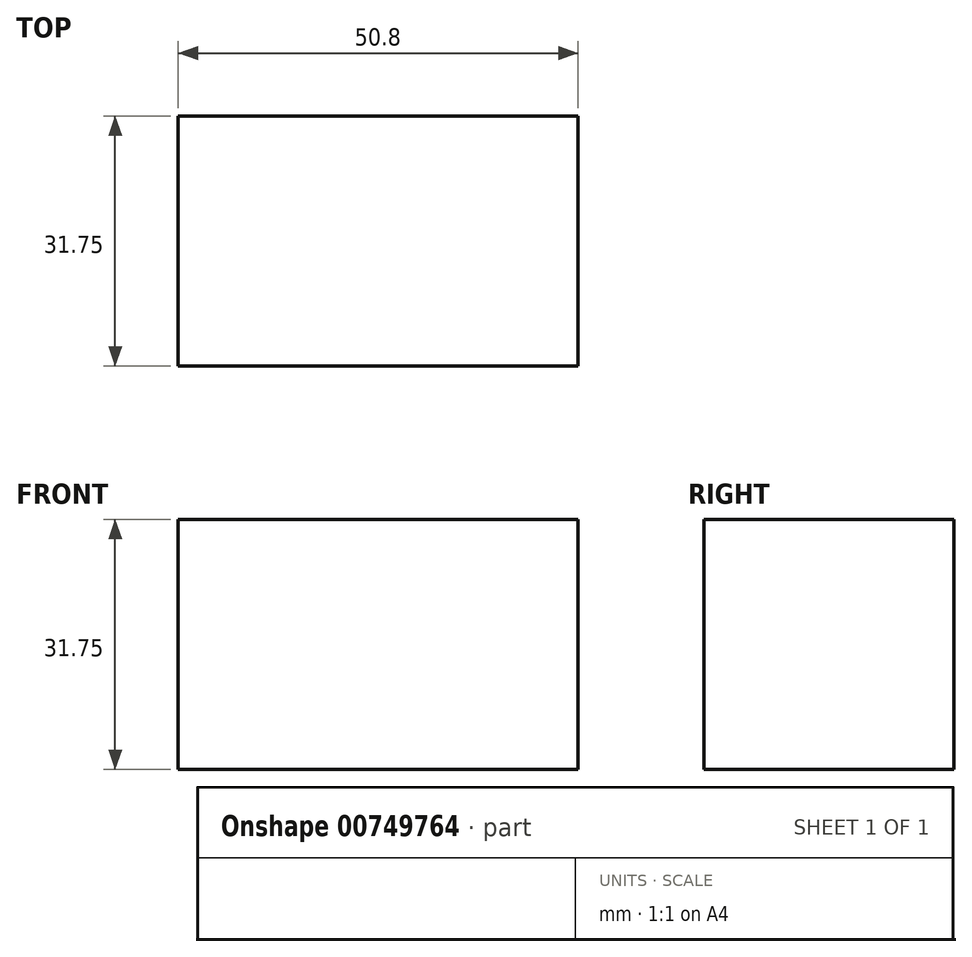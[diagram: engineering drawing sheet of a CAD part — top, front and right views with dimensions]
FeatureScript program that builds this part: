
annotation { "Feature Type Name" : "Feature", "Feature Type Description" : "" }
export const myFeature = defineFeature(function(context is Context, id is Id, definition is map)
    precondition{}
    {
        {
            var Q0;
            Q0=qCreatedBy(makeId("Front.planeOp"),FACE);
            var sketch = newSketch(context, id + "F0", { "sketchPlane" : qUnion([Q0])});
            skLineSegment(sketch, "E0", {"start": v(-26.6, 31.75) * mm, "end": v(-26.6, 0) * mm});
            skLineSegment(sketch, "E1", {"start": v(-26.6, 0) * mm, "end": v(24.2, 0) * mm});
            skLineSegment(sketch, "E2", {"start": v(24.2, 0) * mm, "end": v(24.2, 31.75) * mm});
            skLineSegment(sketch, "E3", {"start": v(24.2, 31.75) * mm, "end": v(-26.6, 31.75) * mm});
            skSolve(sketch);
        }
        {
            var Q0;
            Q0 = qSketchRegion(id + "F0", true);
            extrude(context, id + "F1", {"entities" : qUnion([Q0]), "depth" : 31.75 * mm, "offsetDistance" : 25.4 * mm});
        }
    });
